# Revit family: PRD_FrankeWS_ShwrFttngsPckg_ConnectionSetForShowerPanel_ZSHOW0006
name_source: partatom
category: Pipe Fittings
revit_build: Autodesk Revit 2018 (Build: 20190510_1515(x64)
units: mm (PartAtom-declared; Revit-internal decimal feet)

## family parameters
Always vertical = Yes
Cut with Voids When Loaded = Yes
OmniClass Number = 23.45.55.11
OmniClass Title = Sanitary Components
Part Type = Elbow
Round Connector Dimension = Use Diameter
Shared = No
Work Plane-Based = No

## types (1)
- ZSHOW0006
    AssetType = Fixed
    BIMObjectName = PRD_AR_ShowerFittingsPackage_ConnectionSetForShowerPanel_ZSHOW0006
    BodyMaterial = <By Category>
    Category = Pr_40_20_87_75, Shower fittings package
    Description = Connection set for showerpanel for installed flush-mounting cabinet 195 x 215 mm, consisting of elbow 90°, G 1/2 x G 3/4 B and seal, packing unit 2 pieces.
    DiameterNominal1 = 15  [stored 0.0492126 ft]
    DiameterNominal2 = 20  [stored 0.0656168 ft]
    DurationUnit = year
    GrossWeight = 0.20 kg
    IfcExportAs = IfcSanitaryTerminalType
    IfcExportType = USERDEFINED
    Manufacturer = KWC Group AG
    ManufacturerName = KWC Group AG
    ManufacturerURL = www.kwc.com
    Model = ZSHOW0006
    ModelNumber = 2000104916
    ModelReference = ZSHOW0006
    NBSDescription = Shower fittings package
    NBSReference = 45-35-70/330
    Name = Connection set for shower panel ZSHOW0006
    NetWeight = 0.10 kg
    NominalDepth = 0 mm  [stored 0 ft]
    NominalHeight = 0 mm  [stored 0 ft]
    NominalLength = 0 mm  [stored 0 ft]
    NominalWidth = 0 mm  [stored 0 ft]
    ProductCode = 210.0636.647
    ProductInformation = https://pim.kwc.com
    Quantity = 2
    QuantityUom = Pieces
    Status = New
    TailorMade = No
    URL = www.kwc.com
    Uniclass2015Code = Pr_40_20_87_75
    Uniclass2015Title = Shower fittings package
    Uniclass2015Version = Products v1.23
    Version = 1
    WarrantyDurationUnit = year

note: [stored X ft] marks values corroborated as IEEE doubles in the binary element streams (Revit-internal decimal feet)

## geometry (parser evidence)
native form markers: Sweep x3
no freeform markers — native parametric forms only
